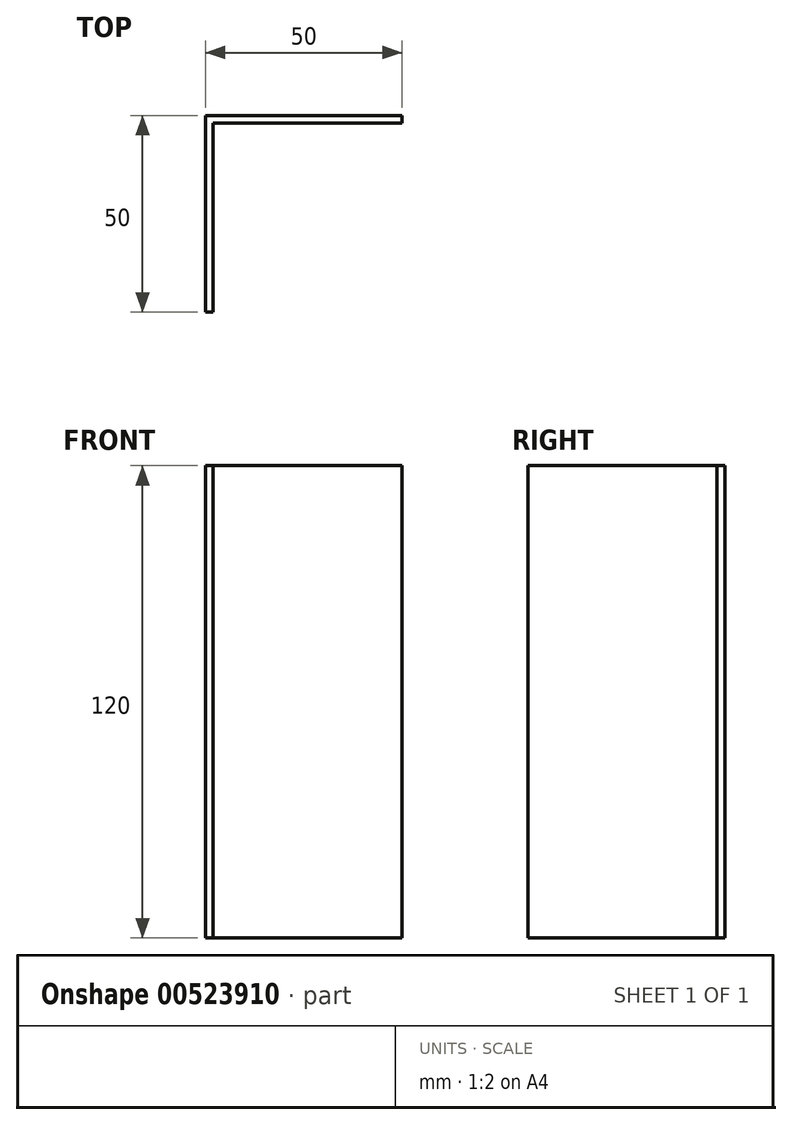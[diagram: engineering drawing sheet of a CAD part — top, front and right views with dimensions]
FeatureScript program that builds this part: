
annotation { "Feature Type Name" : "Feature", "Feature Type Description" : "" }
export const myFeature = defineFeature(function(context is Context, id is Id, definition is map)
    precondition{}
    {
        {
            var Q0;
            Q0=qCreatedBy(makeId("Top.planeOp"),FACE);
            var sketch = newSketch(context, id + "F0", { "sketchPlane" : qUnion([Q0])});
            skLineSegment(sketch, "E0.bottom", {"start": v(0, 2) * mm, "end": v(50, 2) * mm});
            skLineSegment(sketch, "E0.top", {"start": v(0, 0) * mm, "end": v(50, 0) * mm});
            skLineSegment(sketch, "E0.left", {"start": v(0, 2) * mm, "end": v(0, 0) * mm});
            skLineSegment(sketch, "E0.right", {"start": v(50, 2) * mm, "end": v(50, 0) * mm});
            skLineSegment(sketch, "E1.bottom", {"start": v(0, 0) * mm, "end": v(2, 0) * mm});
            skLineSegment(sketch, "E1.top", {"start": v(0, -48) * mm, "end": v(2, -48) * mm});
            skLineSegment(sketch, "E1.left", {"start": v(0, 0) * mm, "end": v(0, -48) * mm});
            skLineSegment(sketch, "E1.right", {"start": v(2, 0) * mm, "end": v(2, -48) * mm});
            skSolve(sketch);
        }
        {
            var Q0;
            Q0 = qSketchRegion(id + "F0", true);
            extrude(context, id + "F1", {"entities" : qUnion([Q0]), "depth" : 120 * mm, "offsetDistance" : 25 * mm});
        }
    });
